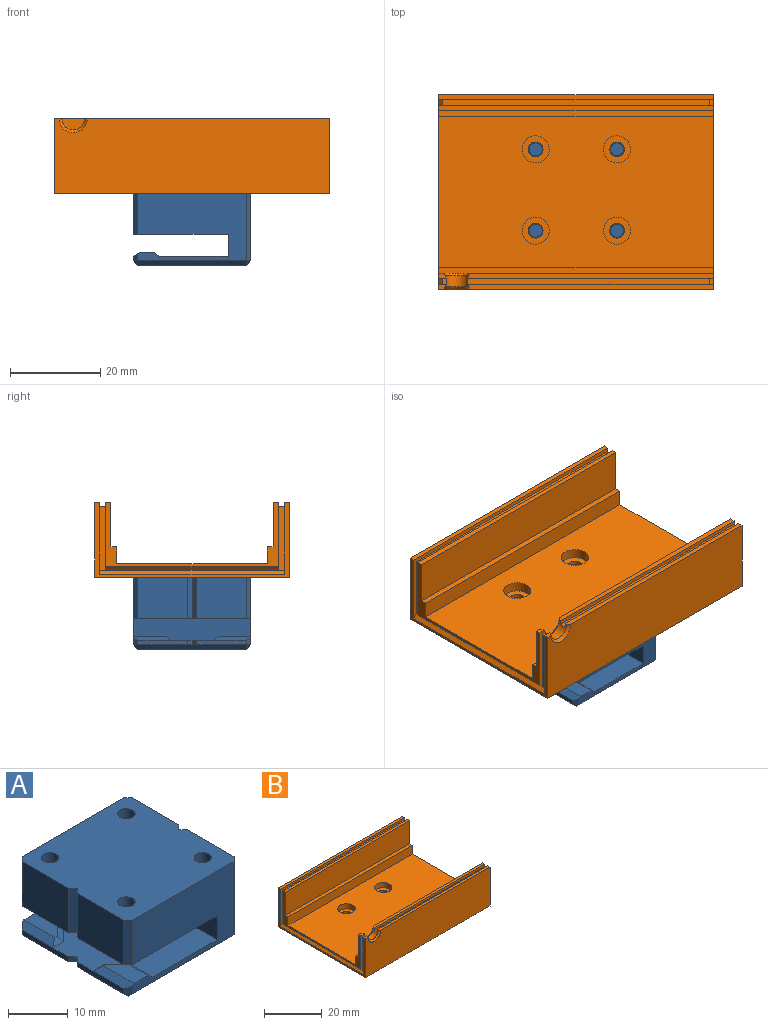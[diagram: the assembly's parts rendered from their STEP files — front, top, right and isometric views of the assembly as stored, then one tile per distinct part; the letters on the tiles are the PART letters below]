
ASSEMBLY  parts=2 mates=1
PART A: 54 faces, bbox 26x26x16 mm
  f0: plane 1x1mm, normal (-0.71,-0.71,0), area 1.4mm2, adj f2,f4,f7,f51
  f1: plane 10x1mm, normal (-0.71,0,-0.71), area 13.4mm2, adj f9,f28,f40,f53
  f2: plane 1x1mm, normal (-0.71,0.71,0), area 1.4mm2, adj f0,f4,f28,f51
  f3: plane 2.5x1mm, normal (0,-0.64,0.77), area 2mm2, adj f4,f13,f15,f16
  f4: plane 26x21mm, normal (0,0,1), area 460.7mm2, adj f0,f2,f3,f6,f7,f11,f13,f14
  f5: plane 11x9.1mm, normal (-1,0,0), area 100.1mm2, adj f10,f12,f23,f24
  f6: plane 24x15mm, normal (0,1,0), area 265.5mm2, adj f4,f10,f11,f12,f14,f15,f16,f19
  f7: plane 11x1mm, normal (-1,0,0), area 11mm2, adj f0,f4,f16,f22,f51
  f8: plane 15x11mm, normal (1,0,0), area 165mm2, adj f10,f17,f18,f19
  f9: plane 24x24mm, normal (0,0,-1), area 478.5mm2, adj f1,f18,f21,f35,f38,f52,f53
  f10: plane 26x26mm, normal (0,0,1), area 645.6mm2, adj f5,f6,f8,f17,f19,f23,f24,f26
  f11: plane 26x4.9mm, normal (-1,0,0), area 127.4mm2, adj f4,f6,f12,f27
  f12: plane 26x21mm, normal (0,0,-1), area 544mm2, adj f5,f6,f11,f23,f24,f26,f27,f41
  f13: plane 3.66x3.66mm, normal (0.45,-0.45,0.77), area 5.5mm2, adj f3,f4,f14,f15
  f14: plane 5x1mm, normal (0.64,0,0.77), area 6.3mm2, adj f4,f6,f13,f15
  f15: plane 7.25x3.3mm, normal (0,0,1), area 20.4mm2, adj f3,f6,f13,f14,f16
  f16: plane 8.25x1.45mm, normal (-0.5,0,0.87), area 12.4mm2, adj f3,f6,f7,f15,f22
  f17: plane 16x1mm, normal (0.71,-0.71,0), area 21.9mm2, adj f8,f10,f18,f34
  f18: plane 12x1mm, normal (0.71,0,-0.71), area 16.3mm2, adj f8,f9,f17,f20
  f19: plane 15x1mm, normal (0.71,0.71,0), area 21.2mm2, adj f6,f8,f10,f20
  f20: plane 1x1mm, normal (0.58,0.58,-0.58), area 0.9mm2, adj f18,f19,f21
  f21: plane 18.5x1mm, normal (0,0.71,-0.71), area 25.5mm2, adj f6,f9,f20,f52
  f22: plane 1.58x1mm, normal (-0.71,0.71,0), area 1.8mm2, adj f6,f7,f16,f51
  f23: plane 9.1x1mm, normal (-0.71,-0.71,0), area 12.9mm2, adj f5,f10,f12,f41
  f24: plane 9.1x1mm, normal (-0.71,0.71,0), area 12.9mm2, adj f5,f6,f10,f12
  f25: plane 2.5x1mm, normal (0,0.64,0.77), area 2mm2, adj f4,f30,f32,f33
  f26: plane 11x9.1mm, normal (-1,0,0), area 100.1mm2, adj f10,f12,f41,f42
  f27: plane 24x15mm, normal (0,-1,0), area 265.5mm2, adj f4,f10,f11,f12,f31,f32,f33,f36
  f28: plane 11x1mm, normal (-1,0,0), area 11mm2, adj f1,f2,f4,f33,f39,f51
  f29: plane 15x11mm, normal (1,0,0), area 165mm2, adj f10,f34,f35,f36
  f30: plane 3.66x3.66mm, normal (0.45,0.45,0.77), area 5.5mm2, adj f4,f25,f31,f32
  f31: plane 5x1mm, normal (0.64,0,0.77), area 6.3mm2, adj f4,f27,f30,f32
  f32: plane 7.25x3.3mm, normal (0,0,1), area 20.4mm2, adj f25,f27,f30,f31,f33
  f33: plane 8.25x1.45mm, normal (-0.5,0,0.87), area 12.4mm2, adj f25,f27,f28,f32,f39
  f34: plane 16x1mm, normal (0.71,0.71,0), area 21.9mm2, adj f10,f17,f29,f35
  f35: plane 12x1mm, normal (0.71,0,-0.71), area 16.3mm2, adj f9,f29,f34,f37
  f36: plane 15x1mm, normal (0.71,-0.71,0), area 21.2mm2, adj f10,f27,f29,f37
  f37: plane 1x1mm, normal (0.58,-0.58,-0.58), area 0.9mm2, adj f35,f36,f38
  f38: plane 24x1mm, normal (0,-0.71,-0.71), area 33.9mm2, adj f9,f27,f37,f40
  f39: plane 1.58x1mm, normal (-0.71,-0.71,0), area 1.8mm2, adj f27,f28,f33,f40
  f40: plane 1x1mm, normal (-0.58,-0.58,-0.58), area 0.9mm2, adj f1,f38,f39
  f41: plane 9.1x1mm, normal (-0.71,0.71,0), area 12.9mm2, adj f10,f12,f23,f26
  f42: plane 9.1x1mm, normal (-0.71,-0.71,0), area 12.9mm2, adj f10,f12,f26,f27
  f43: plane 2.9x2.9mm, normal (0,0,1), area 6.6mm2, adj f44
  f44: cylinder r=1.45mm len=8.6mm, axis (0,0,1), area 78.4mm2, adj f10,f43
  f45: plane 2.9x2.9mm, normal (0,0,1), area 6.6mm2, adj f46
  f46: cylinder r=1.45mm len=8.6mm, axis (0,0,1), area 78.4mm2, adj f10,f45
  f47: plane 2.9x2.9mm, normal (0,0,1), area 6.6mm2, adj f48
  f48: cylinder r=1.45mm len=8.6mm, axis (0,0,1), area 78.4mm2, adj f10,f47
  f49: plane 2.9x2.9mm, normal (0,0,1), area 6.6mm2, adj f50
  f50: cylinder r=1.45mm len=8.6mm, axis (0,0,1), area 78.4mm2, adj f10,f49
  f51: plane 15x6.5mm, normal (0,0,-1), area 96mm2, adj f0,f2,f6,f7,f22,f28,f52,f53
  f52: plane 16x1mm, normal (-0.71,0,-0.71), area 21.2mm2, adj f9,f21,f51,f53
  f53: plane 7.5x1mm, normal (0,0.71,-0.71), area 9.2mm2, adj f1,f9,f51,f52
PART B: 52 faces, bbox 60.8x43.1x16.5 mm
  f0: plane 54.2x1.13mm, normal (0,0,1), area 60.8mm2, adj f2,f13,f18,f37,f39
  f1: plane 54.2x1.13mm, normal (0,0,1), area 60.8mm2, adj f4,f7,f17,f37,f38
  f2: plane 54.35x15.85mm, normal (0,1,0), area 58.5mm2, adj f0,f13,f21,f29,f30,f37
  f3: plane 1.35x0.9mm, normal (0,0,1), area 1.2mm2, adj f28,f31,f32,f37
  f4: plane 54.35x15mm, normal (0,-1,0), area 57.8mm2, adj f1,f7,f27,f29,f30,f37
  f5: plane 60.8x33.3mm, normal (0,0,1), area 1911.5mm2, adj f7,f9,f34,f36,f40,f42,f44,f46
  f6: plane 43.1x16.5mm, normal (-1,0,0), area 63.7mm2, adj f8,f12,f14,f18,f19,f20,f25,f28
  f7: plane 38.15x14.15mm, normal (1,0,0), area 64.8mm2, adj f1,f4,f5,f10,f11,f15,f17,f27
  f8: plane 1.6x1.13mm, normal (0,0,1), area 1.6mm2, adj f6,f18,f28,f37,f39
  f9: plane 38.15x14.15mm, normal (-1,0,0), area 64.8mm2, adj f5,f10,f11,f15,f16,f17,f26,f32
  f10: plane 60.8x15mm, normal (0,1,0), area 75mm2, adj f7,f9,f11,f22,f23,f24,f26,f27
  f11: plane 60.8x1.13mm, normal (0,0,1), area 68.4mm2, adj f7,f9,f10,f15
  f12: plane 60.8x1.13mm, normal (0,0,1), area 68.4mm2, adj f6,f13,f14,f25
  f13: plane 43.1x16.5mm, normal (1,0,0), area 63.7mm2, adj f0,f2,f12,f14,f18,f19,f21,f25
  f14: plane 60.8x16.5mm, normal (0,1,0), area 1003.2mm2, adj f6,f12,f13,f19
  f15: plane 60.8x9.8mm, normal (0,-1,0), area 595.8mm2, adj f7,f9,f11,f33
  f16: plane 1.6x1.13mm, normal (0,0,1), area 1.6mm2, adj f9,f17,f32,f37,f38
  f17: plane 60.8x9.8mm, normal (0,1,0), area 580.7mm2, adj f1,f7,f9,f16,f35,f38
  f18: plane 60.8x16.5mm, normal (0,-1,0), area 988.1mm2, adj f0,f6,f8,f13,f19,f39
  f19: plane 60.8x43.1mm, normal (0,0,-1), area 2587.3mm2, adj f6,f13,f14,f18,f48,f49,f50,f51
  f20: plane 40.85x0.85mm, normal (-0.71,0,0.71), area 49.1mm2, adj f6,f24,f25,f26,f28,f31
  f21: plane 40.85x0.85mm, normal (0.71,0,0.71), area 49.1mm2, adj f2,f13,f22,f25,f27,f29
  f22: plane 14.15x1.35mm, normal (1,0,0), area 19.1mm2, adj f10,f21,f23,f25
  f23: plane 59.1x1.35mm, normal (0,0,1), area 79.8mm2, adj f10,f22,f24,f25
  f24: plane 14.15x1.35mm, normal (-1,0,0), area 19.1mm2, adj f10,f20,f23,f25
  f25: plane 60.8x15.85mm, normal (0,-1,0), area 76.5mm2, adj f6,f12,f13,f20,f21,f22,f23,f24
  f26: plane 38.15x0.85mm, normal (-0.71,0,-0.71), area 45.9mm2, adj f9,f10,f20,f32
  f27: plane 38.15x0.85mm, normal (0.71,0,-0.71), area 45.9mm2, adj f4,f7,f10,f21
  f28: plane 15.85x1.75mm, normal (0,1,0), area 13.8mm2, adj f3,f6,f8,f20,f31,f37
  f29: plane 14.15x1.35mm, normal (1,0,0), area 19.1mm2, adj f2,f4,f21,f30
  f30: plane 53.5x1.35mm, normal (0,0,1), area 72.2mm2, adj f2,f4,f29,f37
  f31: plane 14.15x1.35mm, normal (-1,0,0), area 19.1mm2, adj f3,f20,f28,f32
  f32: plane 15x1.75mm, normal (0,-1,0), area 13.1mm2, adj f3,f9,f16,f26,f31,f37
  f33: plane 60.8x1.3mm, normal (0,0,1), area 79mm2, adj f7,f9,f15,f34
  f34: plane 60.8x3.7mm, normal (0,-1,0), area 225mm2, adj f5,f7,f9,f33
  f35: plane 60.8x1.3mm, normal (0,0,1), area 79mm2, adj f7,f9,f17,f36
  f36: plane 60.8x3.7mm, normal (0,1,0), area 225mm2, adj f5,f7,f9,f35
  f37: cylinder r=2.5mm len=5mm, axis (0,-1,0), area 16.5mm2, adj f0,f1,f2,f3,f4,f8,f16,f28
  f38: cone r=3.1mm half-angle=45deg, axis (0,1,0), area 7.5mm2, adj f1,f16,f17,f37
  f39: cone r=2.5mm half-angle=45deg, axis (0,-1,0), area 7.5mm2, adj f0,f8,f18,f37
  f40: cylinder r=3mm len=6mm, axis (0,0,1), area 41.5mm2, adj f5,f41
  f41: plane 6x6mm, normal (0,0,1), area 20mm2, adj f40,f51
  f42: cylinder r=3mm len=6mm, axis (0,0,1), area 41.5mm2, adj f5,f43
  f43: plane 6x6mm, normal (0,0,1), area 20mm2, adj f42,f50
  f44: cylinder r=3mm len=6mm, axis (0,0,1), area 41.5mm2, adj f5,f45
  f45: plane 6x6mm, normal (0,0,1), area 20mm2, adj f44,f49
  f46: cylinder r=3mm len=6mm, axis (0,0,1), area 41.5mm2, adj f5,f47
  f47: plane 6x6mm, normal (0,0,1), area 20mm2, adj f46,f48
  f48: cylinder r=1.62mm len=3.25mm, axis (0,0,1), area 8.2mm2, adj f19,f47
  f49: cylinder r=1.62mm len=3.25mm, axis (0,0,1), area 8.2mm2, adj f19,f45
  f50: cylinder r=1.62mm len=3.25mm, axis (0,0,1), area 8.2mm2, adj f19,f43
  f51: cylinder r=1.62mm len=3.25mm, axis (0,0,1), area 8.2mm2, adj f19,f41
PLACE A t=(-8.37,5.67,-1.76)mm
PLACE B t=(-24.67,-11.88,19.24)mm
MATE planar B.f19 <-> A.f10  axis (0,0,-1) through (4.63,5.67,12.24)mm
